# Revit family: LWPLIFE-PRO_Non Hosted_R16
name_source: partatom
category: Lighting Fixtures
revit_build: Autodesk Revit 2017 (Build: 20160225_1515(x64)
units: mm (PartAtom-declared; Revit-internal decimal feet)

## family parameters
Always vertical = Yes
Cut with Voids When Loaded = No
Light Source = Yes
OmniClass Number = 23.80.70.00
OmniClass Title = Lighting
Part Type = Normal
Room Calculation Point = No
Round Connector Dimension = Use Diameter
Shared = No
Work Plane-Based = No

## types (1)
- LWPLIFE-PRO
    AS2293 = C0=D32    C90=D32
    Apparent Load = 0 VA
    Charging Method = Intelligent current limited constant voltage
    Color Filter = 16777215
    Dimming Lamp Color Temperature Shift = <None>
    Emit Shape Visible in Rendering = No
    Emit from Circle Diameter = 610 mm
    IP Rating = IP66/67
    Lamp = 2 x 3W LED (Lifetime wa
2 x 3W LED (Lifetime warranty on the lamp head and loom assembly)
    Mounting = Surface Mount IP66/67 with integral lamp head, charger pack & battery
    Operating Mode = Non-Maintained
    Operating Temperature = 0°C to 40°C (Ambient)
    Operating Voltage = 240.00 V
    Photometric Web File = ll16297 - LWPLIFE-PRO-ZW.IES
    Power Consumption = 0.40 W
    Testing System = N/A – Manual Test Switch
    Tilt Angle = 90.00°

## geometry (parser evidence)
native form markers: Sweep x2
no freeform markers — native parametric forms only
